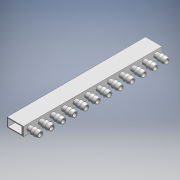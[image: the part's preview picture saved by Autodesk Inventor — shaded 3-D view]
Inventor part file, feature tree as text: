
AUTODESK INVENTOR PART (.ipt)
format: ipt  version: 2018 (Build 220112000, 112)  size: 268,800 bytes
history: native  units: in
note: dims shown in document units (in); Inventor stores cm internally (conversion verified against a paired STEP export)
features: other x7, extrude x4, sketch x2, pattern_linear x1, projected_geometry x1
ambient origin geometry x8: Origin, YZ Plane, XZ Plane, XY Plane, X Axis, Y Axis, Z Axis, Center Point
bodies: Body1 (feature_tree)
feature tree (15):
  other  "CrossSection1"
  other  "Silicone Fitting Plane"
  other  "Cap Plane"
  other  "Base Sketch"
  extrude  "Base"  Depth=0.0591in
  other  "Silicone Fitting"
  extrude  "Airflow Cut"  Depth=0.0591in
  pattern_linear  "Fitting Repetitions"  Spacing1=0.0197in  [1 undecoded]
  sketch  "Sketch22"  dims[d87=0.0197in d88=0.0787in d89=-1.0625in d90=0.7874in d1=0.0591in]
  extrude  "Extrusion21"  Depth=0.5906in
  extrude  "Extrusion24"  [1 undecoded]
  other  "Silicone Fitting Sketch"
  other  "Airflow Cut Sketch"
  projected_geometry  "Projected Loop7"
  sketch  "Sketch23"  dims[d2=0.0591in d3=0.0591in d4=0.0197in d5=0.5906in d6=-0.2067in d7=4.9606in d8=0.0in d111=90.0deg d112=0.0787in d9=0.0in d10=4.7244in d11=0.4134in d12=-4.9606in d141=0.0295in d142=0.0295in d143=0.2623in d144=0.502in d145=0.0591in d146=0.0295in d147=0.0295in d148=0.0295in d149=0.4134in d150=0.0in d155=0.0591in d156=0.0in]
note: 2 required parameter values undecoded (feature->parameter linkage not recoverable at this tier; creation-order binding heuristic only, values carry confidence <= 0.55)
